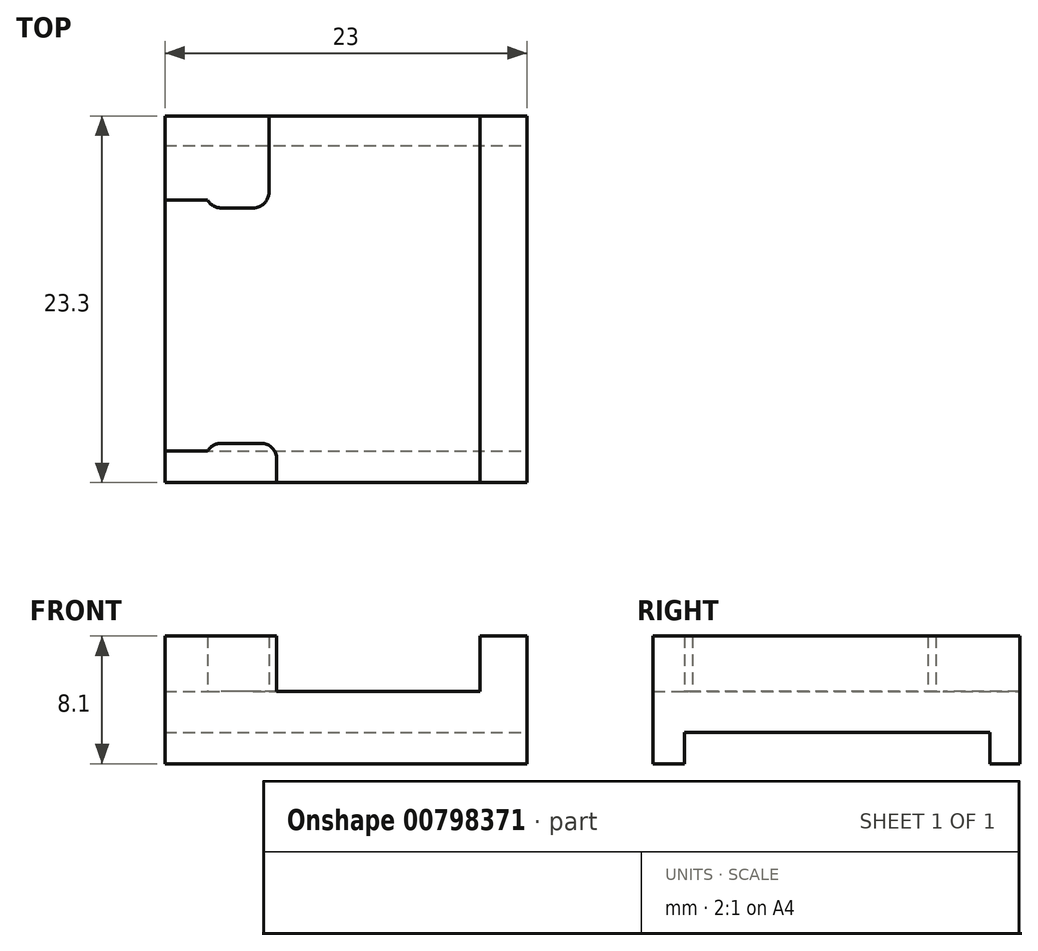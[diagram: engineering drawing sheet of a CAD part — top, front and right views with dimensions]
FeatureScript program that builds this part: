
annotation { "Feature Type Name" : "Feature", "Feature Type Description" : "" }
export const myFeature = defineFeature(function(context is Context, id is Id, definition is map)
    precondition{}
    {
        {
            var Q0;
            Q0=qCreatedBy(makeId("Top.planeOp"),FACE);
            var sketch = newSketch(context, id + "F0", { "sketchPlane" : qUnion([Q0])});
            skLineSegment(sketch, "E0.bottom", {"start": v(0, 0) * mm, "end": v(23, 0) * mm});
            skLineSegment(sketch, "E0.top", {"start": v(0, -23.3) * mm, "end": v(23, -23.3) * mm});
            skLineSegment(sketch, "E0.left", {"start": v(0, 0) * mm, "end": v(0, -23.3) * mm});
            skLineSegment(sketch, "E0.right", {"start": v(23, 0) * mm, "end": v(23, -23.3) * mm});
            skLineSegment(sketch, "E1", {"start": v(20, -23.3) * mm, "end": v(20, 0) * mm});
            skLineSegment(sketch, "E2.bottom", {"start": v(0, 0) * mm, "end": v(6.6, 0) * mm});
            skLineSegment(sketch, "E2.top", {"start": v(0, -5.35) * mm, "end": v(6.6, -5.35) * mm});
            skLineSegment(sketch, "E2.left", {"start": v(0, 0) * mm, "end": v(0, -5.35) * mm});
            skLineSegment(sketch, "E2.right", {"start": v(6.6, 0) * mm, "end": v(6.6, -5.35) * mm});
            skLineSegment(sketch, "E3.bottom", {"start": v(0, -23.3) * mm, "end": v(7.1, -23.3) * mm});
            skLineSegment(sketch, "E3.top", {"start": v(0, -21.3) * mm, "end": v(7.1, -21.3) * mm});
            skLineSegment(sketch, "E3.left", {"start": v(0, -23.3) * mm, "end": v(0, -21.3) * mm});
            skLineSegment(sketch, "E3.right", {"start": v(7.1, -23.3) * mm, "end": v(7.1, -21.3) * mm});
            skLineSegment(sketch, "E4.bottom", {"start": v(7.1, -21.3) * mm, "end": v(2.7, -21.3) * mm});
            skLineSegment(sketch, "E4.top", {"start": v(7.1, -20.8) * mm, "end": v(2.7, -20.8) * mm});
            skLineSegment(sketch, "E4.left", {"start": v(7.1, -21.3) * mm, "end": v(7.1, -20.8) * mm});
            skLineSegment(sketch, "E4.right", {"start": v(2.7, -21.3) * mm, "end": v(2.7, -20.8) * mm});
            skLineSegment(sketch, "E5.bottom", {"start": v(6.6, -5.35) * mm, "end": v(2.7, -5.35) * mm});
            skLineSegment(sketch, "E5.top", {"start": v(6.6, -5.85) * mm, "end": v(2.7, -5.85) * mm});
            skLineSegment(sketch, "E5.left", {"start": v(6.6, -5.35) * mm, "end": v(6.6, -5.85) * mm});
            skLineSegment(sketch, "E5.right", {"start": v(2.7, -5.35) * mm, "end": v(2.7, -5.85) * mm});
            skSolve(sketch);
        }
        {
            var Q0;
            {var subQ10=sQuery(id+"F0.wireOp",EDGE,"E1");Q0=makeQuery(id+"F0.imprint","IMPRINT",FACE,{"disambiguationData":[TD([[makeQuery(id+"F0.imprint","IMPRINT",EDGE,{"derivedFrom":subQ10}),1.0]])]});}
            extrude(context, id + "F1", {"entities" : qUnion([Q0]), "depth" : 2.6 * mm, "offsetDistance" : 25 * mm});
        }
        {
            var Q0;
            {var subQ0=sQuery(id+"F0.wireOp",EDGE,"E0.right");Q0=makeQuery(id+"F0.imprint","IMPRINT",FACE,{"disambiguationData":[TD([[makeQuery(id+"F0.imprint","IMPRINT",EDGE,{"derivedFrom":subQ0}),-1.0]])]});}
            var Q1;
            {var subQ4=sQuery(id+"F0.wireOp",EDGE,"E3.right");Q1=makeQuery(id+"F0.imprint","IMPRINT",FACE,{"disambiguationData":[TD([[makeQuery(id+"F0.imprint","IMPRINT",EDGE,{"derivedFrom":subQ4}),1.0]])]});}
            var Q2;
            {var subQ4=sQuery(id+"F0.wireOp",EDGE,"E2.right");Q2=makeQuery(id+"F0.imprint","IMPRINT",FACE,{"disambiguationData":[TD([[makeQuery(id+"F0.imprint","IMPRINT",EDGE,{"derivedFrom":subQ4}),-1.0]])]});}
            var Q3;
            Q3=makeQuery(id+"F0.imprint","IMPRINT",FACE,{"disambiguationData":[TD([[makeQuery(id+"F0.imprint","IMPRINT",EDGE,{"derivedFrom":sQuery(id+"F0.wireOp",EDGE,"E4.top")}),1.0]])]});
            var Q4;
            Q4=makeQuery(id+"F0.imprint","IMPRINT",FACE,{"disambiguationData":[TD([[makeQuery(id+"F0.imprint","IMPRINT",EDGE,{"derivedFrom":sQuery(id+"F0.wireOp",EDGE,"E5.top")}),-1.0]])]});
            extrude(context, id + "F2", {"entities" : qUnion([Q0, Q1, Q2, Q3, Q4]), "operationType" : NewBodyOperationType.ADD, "depth" : 6.1 * mm, "offsetDistance" : 25 * mm});
        }
        {
            var Q0;
            Q0=makeQuery(id+"F2.opExtrude","SWEPT_EDGE",EDGE,{"disambiguationData":[OSD([sQuery(id+"F0.wireOp",EDGE,"E4.top"),sQuery(id+"F0.wireOp",EDGE,"E4.left")])]});
            var Q1;
            Q1=makeQuery(id+"F2.opExtrude","SWEPT_EDGE",EDGE,{"disambiguationData":[OSD([sQuery(id+"F0.wireOp",EDGE,"E4.top"),sQuery(id+"F0.wireOp",EDGE,"E4.right")])]});
            var Q2;
            Q2=makeQuery(id+"F2.opExtrude","SWEPT_EDGE",EDGE,{"disambiguationData":[OSD([sQuery(id+"F0.wireOp",EDGE,"E5.top"),sQuery(id+"F0.wireOp",EDGE,"E5.left")])]});
            var Q3;
            Q3=makeQuery(id+"F2.opExtrude","SWEPT_EDGE",EDGE,{"disambiguationData":[OSD([sQuery(id+"F0.wireOp",EDGE,"E5.top"),sQuery(id+"F0.wireOp",EDGE,"E5.right")])]});
            fillet(context, id + "F3", {"entities" : qUnion([Q0, Q1, Q2, Q3]), "radius" : 1 * mm, "tangentPropagation" : true, "allowEdgeOverflow" : false});
        }
        {
            var Q0;
            Q0=qCreatedBy(makeId("Top.planeOp"),FACE);
            var sketch = newSketch(context, id + "F4", { "sketchPlane" : qUnion([Q0])});
            skLineSegment(sketch, "E6.bottom", {"start": v(0, -23.3) * mm, "end": v(23, -23.3) * mm});
            skLineSegment(sketch, "E6.top", {"start": v(0, -21.3) * mm, "end": v(23, -21.3) * mm});
            skLineSegment(sketch, "E6.left", {"start": v(0, -23.3) * mm, "end": v(0, -21.3) * mm});
            skLineSegment(sketch, "E6.right", {"start": v(23, -23.3) * mm, "end": v(23, -21.3) * mm});
            skLineSegment(sketch, "E7.bottom", {"start": v(0, 0) * mm, "end": v(23, 0) * mm});
            skLineSegment(sketch, "E7.top", {"start": v(0, -1.9) * mm, "end": v(23, -1.9) * mm});
            skLineSegment(sketch, "E7.left", {"start": v(0, 0) * mm, "end": v(0, -1.9) * mm});
            skLineSegment(sketch, "E7.right", {"start": v(23, 0) * mm, "end": v(23, -1.9) * mm});
            skSolve(sketch);
        }
        {
            var Q0;
            Q0 = qSketchRegion(id + "F4", true);
            extrude(context, id + "F5", {"entities" : qUnion([Q0]), "operationType" : NewBodyOperationType.ADD, "oppositeDirection" : true, "depth" : 2 * mm, "offsetDistance" : 25 * mm});
        }
    });
